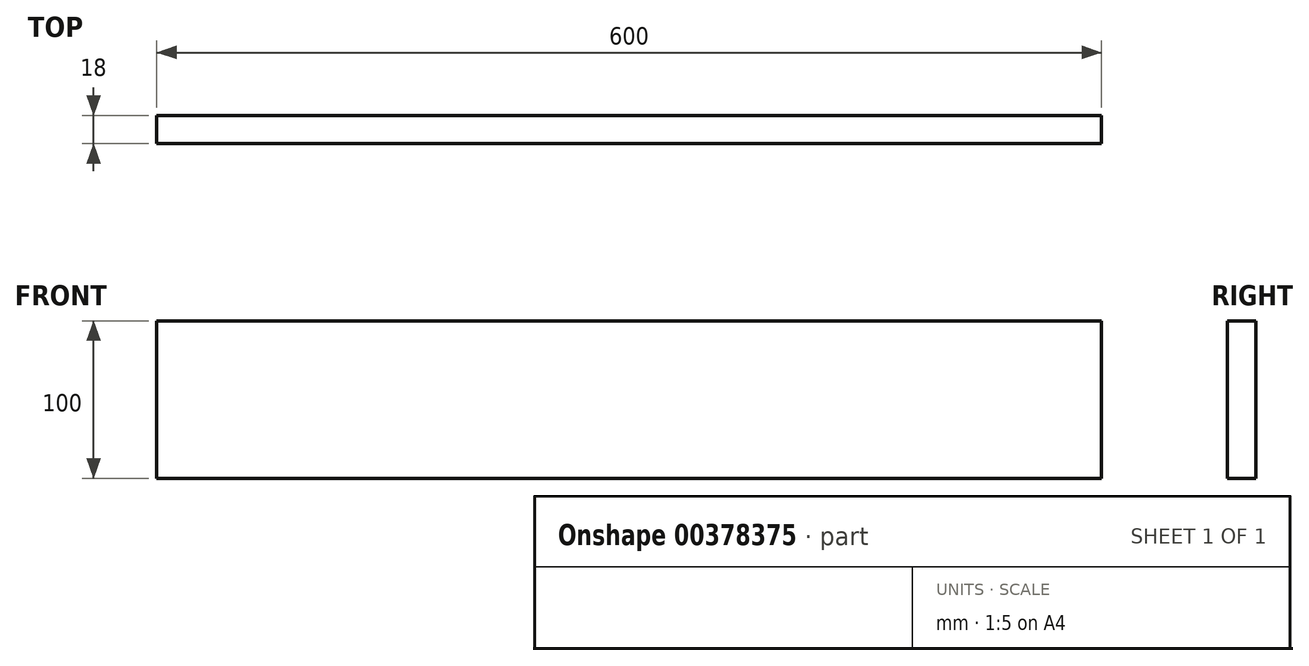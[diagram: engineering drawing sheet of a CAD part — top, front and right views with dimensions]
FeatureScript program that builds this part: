
annotation { "Feature Type Name" : "Feature", "Feature Type Description" : "" }
export const myFeature = defineFeature(function(context is Context, id is Id, definition is map)
    precondition{}
    {
        {
            var Q0;
            Q0=qCreatedBy(makeId("Right.planeOp"),FACE);
            var sketch = newSketch(context, id + "F0", { "sketchPlane" : qUnion([Q0])});
            skLineSegment(sketch, "E0.bottom", {"start": v(9, 50) * mm, "end": v(-9, 50) * mm});
            skLineSegment(sketch, "E0.top", {"start": v(9, -50) * mm, "end": v(-9, -50) * mm});
            skLineSegment(sketch, "E0.left", {"start": v(9, 50) * mm, "end": v(9, -50) * mm});
            skLineSegment(sketch, "E0.right", {"start": v(-9, 50) * mm, "end": v(-9, -50) * mm});
            skPoint(sketch, "E0.middle", {"position": v(0, 0) * mm});
            skSolve(sketch);
        }
        {
            var Q0;
            Q0=qSketchRegion(id+"F0",true);
            extrude(context, id + "F1", {"entities" : qUnion([Q0]), "depth" : 600 * mm});
        }
    });
